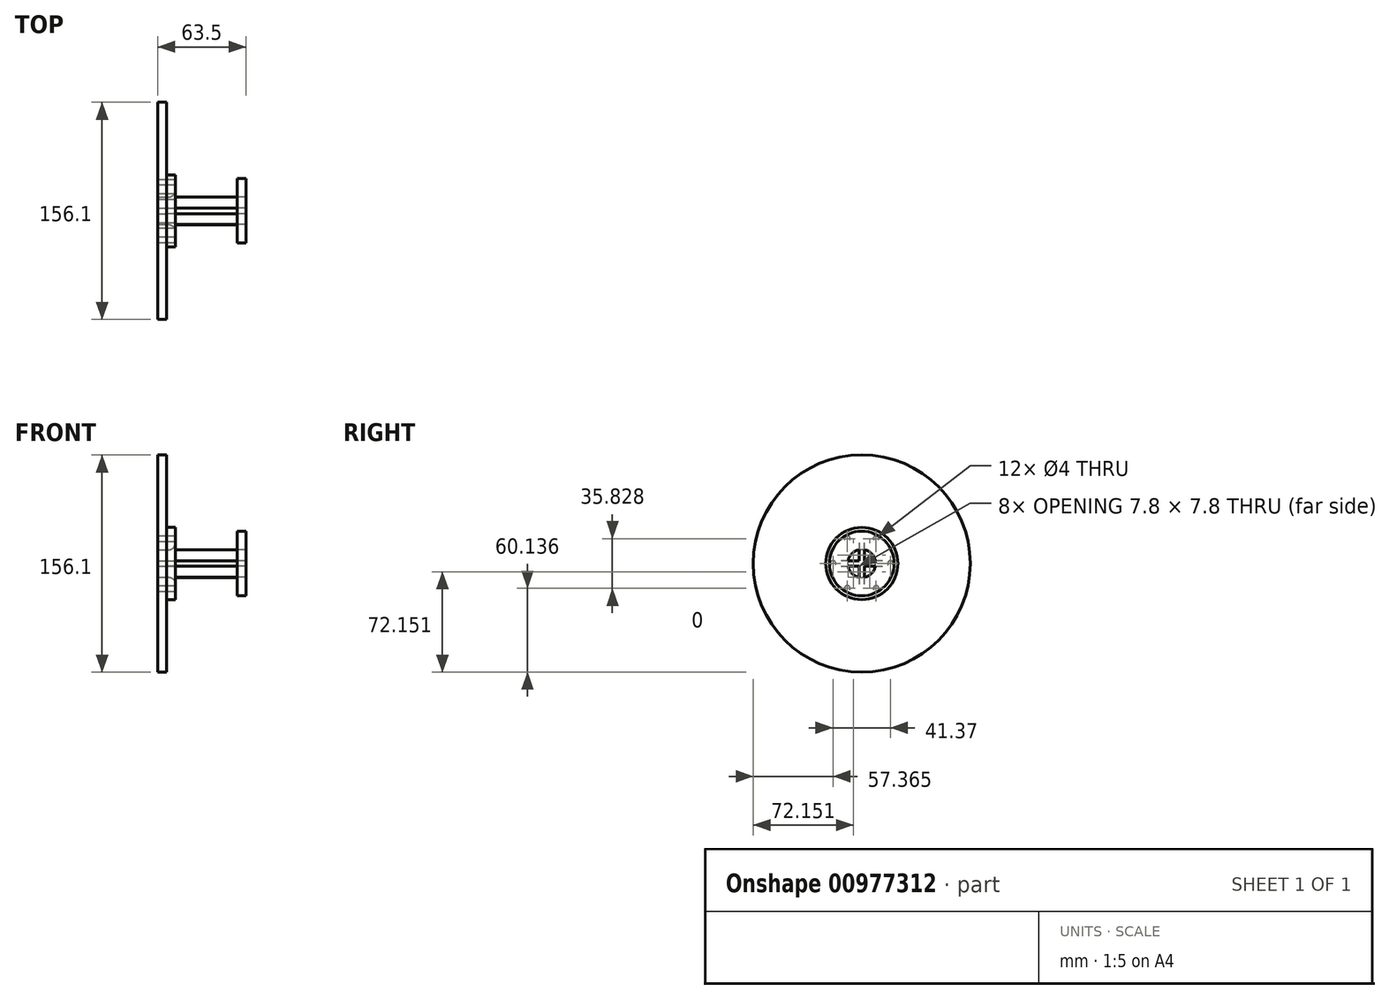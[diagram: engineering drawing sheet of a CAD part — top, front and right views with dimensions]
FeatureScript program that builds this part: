
annotation { "Feature Type Name" : "Feature", "Feature Type Description" : "" }
export const myFeature = defineFeature(function(context is Context, id is Id, definition is map)
    precondition{}
    {
        {
            var Q0;
            Q0=qCreatedBy(makeId("Right.planeOp"),FACE);
            var sketch = newSketch(context, id + "F0", { "sketchPlane" : qUnion([Q0])});
            skCircle(sketch, "E0", {"center": v(0, 0) * mm, "radius": 10 * mm});
            skLineSegment(sketch, "E1.bottom", {"start": v(2, 12.5) * mm, "end": v(-2, 12.5) * mm});
            skLineSegment(sketch, "E1.top", {"start": v(2, -12.5) * mm, "end": v(-2, -12.5) * mm});
            skLineSegment(sketch, "E1.left", {"start": v(2, 12.5) * mm, "end": v(2, -12.5) * mm});
            skLineSegment(sketch, "E1.right", {"start": v(-2, 12.5) * mm, "end": v(-2, -12.5) * mm});
            skLineSegment(sketch, "E2.bottom", {"start": v(12.5, 2) * mm, "end": v(-12.5, 2) * mm});
            skLineSegment(sketch, "E2.top", {"start": v(12.5, -2) * mm, "end": v(-12.5, -2) * mm});
            skLineSegment(sketch, "E2.left", {"start": v(12.5, 2) * mm, "end": v(12.5, -2) * mm});
            skLineSegment(sketch, "E2.right", {"start": v(-12.5, 2) * mm, "end": v(-12.5, -2) * mm});
            skLineSegment(sketch, "E3.bottom", {"start": v(2, 8) * mm, "end": v(-2, 8) * mm});
            skLineSegment(sketch, "E3.top", {"start": v(2, -8) * mm, "end": v(-2, -8) * mm});
            skLineSegment(sketch, "E4", {"start": v(-8, 2) * mm, "end": v(-8, -2) * mm});
            skLineSegment(sketch, "E5", {"start": v(8, 2) * mm, "end": v(8, -2) * mm});
            skCircle(sketch, "E6", {"center": v(0, 0) * mm, "radius": 25.94 * mm});
            skPoint(sketch, "E7", {"position": v(32.91, 0) * mm});
            skPoint(sketch, "E8", {"position": v(20.69, 0) * mm});
            skCircle(sketch, "E9.cCircle", {"center": v(0, 0) * mm, "radius": 20.69 * mm, "construction": true});
            skLineSegment(sketch, "E9.0", {"start": v(20.69, 0) * mm, "end": v(10.34, -17.91) * mm});
            skLineSegment(sketch, "E9.1", {"start": v(10.34, -17.91) * mm, "end": v(-10.34, -17.91) * mm});
            skLineSegment(sketch, "E9.2", {"start": v(-10.34, -17.91) * mm, "end": v(-20.69, 0) * mm});
            skLineSegment(sketch, "E9.3", {"start": v(-20.69, 0) * mm, "end": v(-10.34, 17.91) * mm});
            skLineSegment(sketch, "E9.4", {"start": v(-10.34, 17.91) * mm, "end": v(10.34, 17.91) * mm});
            skLineSegment(sketch, "E9.5", {"start": v(10.34, 17.91) * mm, "end": v(20.69, 0) * mm});
            skSolve(sketch);
        }
        {
            var Q0;
            {var subQ2=sQuery(id+"F0.wireOp",EDGE,"E0");var subQ4=sQuery(id+"F0.wireOp",EDGE,"E1.left");var subQ6=makeQuery(id+"F0.imprint","INTERSECT",VERTEX,{"disambiguationData":[OD(1.0)],"derivedFrom":[subQ2,subQ4]});Q0=makeQuery(id+"F0.imprint","IMPRINT",FACE,{"disambiguationData":[TD([[makeQuery(id+"F0.imprint","IMPRINT",EDGE,{"disambiguationData":[TD([[subQ6,-1.0]])],"derivedFrom":subQ2}),1.0]])]});}
            var Q1;
            {var subQ0=sQuery(id+"F0.wireOp",EDGE,"E2.top");var subQ5=sQuery(id+"F0.wireOp",EDGE,"E0");var subQ7=makeQuery(id+"F0.imprint","INTERSECT",VERTEX,{"disambiguationData":[OD(0.0)],"derivedFrom":[subQ5,subQ0]});Q1=makeQuery(id+"F0.imprint","IMPRINT",FACE,{"disambiguationData":[TD([[makeQuery(id+"F0.imprint","IMPRINT",EDGE,{"disambiguationData":[TD([[subQ7,-1.0]])],"derivedFrom":subQ5}),1.0]])]});}
            var Q2;
            {var subQ0=sQuery(id+"F0.wireOp",EDGE,"E1.right");var subQ5=sQuery(id+"F0.wireOp",EDGE,"E0");var subQ6=makeQuery(id+"F0.imprint","INTERSECT",VERTEX,{"disambiguationData":[OD(0.0)],"derivedFrom":[subQ5,subQ0]});Q2=makeQuery(id+"F0.imprint","IMPRINT",FACE,{"disambiguationData":[TD([[makeQuery(id+"F0.imprint","IMPRINT",EDGE,{"disambiguationData":[TD([[subQ6,-1.0]])],"derivedFrom":subQ5}),1.0]])]});}
            var Q3;
            {var subQ0=sQuery(id+"F0.wireOp",EDGE,"E1.left");var subQ4=sQuery(id+"F0.wireOp",EDGE,"E0");var subQ5=makeQuery(id+"F0.imprint","INTERSECT",VERTEX,{"disambiguationData":[OD(0.0)],"derivedFrom":[subQ4,subQ0]});Q3=makeQuery(id+"F0.imprint","IMPRINT",FACE,{"disambiguationData":[TD([[makeQuery(id+"F0.imprint","IMPRINT",EDGE,{"disambiguationData":[TD([[subQ5,1.0]])],"derivedFrom":subQ4}),1.0]])]});}
            var Q4;
            {var subQ5=sQuery(id+"F0.wireOp",EDGE,"E5");Q4=makeQuery(id+"F0.imprint","IMPRINT",FACE,{"disambiguationData":[TD([[makeQuery(id+"F0.imprint","IMPRINT",EDGE,{"derivedFrom":subQ5}),-1.0]])]});}
            var Q5;
            {var subQ0=sQuery(id+"F0.wireOp",EDGE,"E2.bottom");var subQ1=sQuery(id+"F0.wireOp",EDGE,"E1.left");var subQ2=makeQuery(id+"F0.imprint","INTERSECT",VERTEX,{"derivedFrom":[subQ1,subQ0]});Q5=makeQuery(id+"F0.imprint","IMPRINT",FACE,{"disambiguationData":[TD([[makeQuery(id+"F0.imprint","IMPRINT",EDGE,{"disambiguationData":[TD([[subQ2,-1.0]])],"derivedFrom":subQ1}),-1.0]])]});}
            var Q6;
            {var subQ0=sQuery(id+"F0.wireOp",EDGE,"E3.bottom");Q6=makeQuery(id+"F0.imprint","IMPRINT",FACE,{"disambiguationData":[TD([[makeQuery(id+"F0.imprint","IMPRINT",EDGE,{"derivedFrom":subQ0}),1.0]])]});}
            var Q7;
            {var subQ5=sQuery(id+"F0.wireOp",EDGE,"E4");Q7=makeQuery(id+"F0.imprint","IMPRINT",FACE,{"disambiguationData":[TD([[makeQuery(id+"F0.imprint","IMPRINT",EDGE,{"derivedFrom":subQ5}),1.0]])]});}
            var Q8;
            {var subQ0=sQuery(id+"F0.wireOp",EDGE,"E3.top");Q8=makeQuery(id+"F0.imprint","IMPRINT",FACE,{"disambiguationData":[TD([[makeQuery(id+"F0.imprint","IMPRINT",EDGE,{"derivedFrom":subQ0}),-1.0]])]});}
            var Q9;
            {var subQ5=sQuery(id+"F0.wireOp",EDGE,"E4");Q9=makeQuery(id+"F0.imprint","IMPRINT",FACE,{"disambiguationData":[TD([[makeQuery(id+"F0.imprint","IMPRINT",EDGE,{"derivedFrom":subQ5}),-1.0]])]});}
            var Q10;
            {var subQ5=sQuery(id+"F0.wireOp",EDGE,"E3.top");Q10=makeQuery(id+"F0.imprint","IMPRINT",FACE,{"disambiguationData":[TD([[makeQuery(id+"F0.imprint","IMPRINT",EDGE,{"derivedFrom":subQ5}),1.0]])]});}
            var Q11;
            {var subQ5=sQuery(id+"F0.wireOp",EDGE,"E5");Q11=makeQuery(id+"F0.imprint","IMPRINT",FACE,{"disambiguationData":[TD([[makeQuery(id+"F0.imprint","IMPRINT",EDGE,{"derivedFrom":subQ5}),1.0]])]});}
            var Q12;
            {var subQ5=sQuery(id+"F0.wireOp",EDGE,"E3.bottom");Q12=makeQuery(id+"F0.imprint","IMPRINT",FACE,{"disambiguationData":[TD([[makeQuery(id+"F0.imprint","IMPRINT",EDGE,{"derivedFrom":subQ5}),-1.0]])]});}
            extrude(context, id + "F1", {"entities" : qUnion([Q0, Q1, Q2, Q3, Q4, Q5, Q6, Q7, Q8, Q9, Q10, Q11, Q12]), "depth" : 50.8 * mm, "offsetDistance" : 25.4 * mm});
        }
        {
            var Q0;
            {var subQ10=sQuery(id+"F0.wireOp",EDGE,"E1.bottom");Q0=makeQuery(id+"F0.imprint","IMPRINT",FACE,{"disambiguationData":[TD([[makeQuery(id+"F0.imprint","IMPRINT",EDGE,{"derivedFrom":subQ10}),-1.0]])]});}
            var Q1;
            Q1=makeQuery(id+"F0.imprint","IMPRINT",FACE,{"disambiguationData":[TD([[makeQuery(id+"F0.imprint","IMPRINT",EDGE,{"derivedFrom":sQuery(id+"F0.wireOp",EDGE,"E6")}),1.0]])]});
            var Q2;
            {var subQ5=sQuery(id+"F0.wireOp",EDGE,"E1.bottom");Q2=makeQuery(id+"F0.imprint","IMPRINT",FACE,{"disambiguationData":[TD([[makeQuery(id+"F0.imprint","IMPRINT",EDGE,{"derivedFrom":subQ5}),1.0]])]});}
            var Q3;
            {var subQ5=sQuery(id+"F0.wireOp",EDGE,"E2.left");Q3=makeQuery(id+"F0.imprint","IMPRINT",FACE,{"disambiguationData":[TD([[makeQuery(id+"F0.imprint","IMPRINT",EDGE,{"derivedFrom":subQ5}),-1.0]])]});}
            var Q4;
            {var subQ5=sQuery(id+"F0.wireOp",EDGE,"E2.right");Q4=makeQuery(id+"F0.imprint","IMPRINT",FACE,{"disambiguationData":[TD([[makeQuery(id+"F0.imprint","IMPRINT",EDGE,{"derivedFrom":subQ5}),1.0]])]});}
            var Q5;
            {var subQ5=sQuery(id+"F0.wireOp",EDGE,"E1.top");Q5=makeQuery(id+"F0.imprint","IMPRINT",FACE,{"disambiguationData":[TD([[makeQuery(id+"F0.imprint","IMPRINT",EDGE,{"derivedFrom":subQ5}),-1.0]])]});}
            extrude(context, id + "F2", {"entities" : qUnion([Q0, Q1, Q2, Q3, Q4, Q5]), "operationType" : NewBodyOperationType.ADD, "depth" : 6.35 * mm, "offsetDistance" : 25.4 * mm});
        }
        {
            var Q0;
            {var subQ0=sQuery(id+"F0.wireOp",EDGE,"E0");Q0=makeQuery(id+"F2.boolean.opBoolean","MERGE",FACE,{"derivedFrom":[makeQuery(id+"F1.opExtrude","CAP_FACE",FACE,{"disambiguationData":[OSD([subQ0])],"isStart":true}),makeQuery(id+"F2.opExtrude","CAP_FACE",FACE,{"disambiguationData":[OSD([subQ0,sQuery(id+"F0.wireOp",EDGE,"E6")])],"isStart":true})]});}
            var sketch = newSketch(context, id + "F3", { "sketchPlane" : qUnion([Q0])});
            skCircle(sketch, "E10", {"center": v(0, 0) * mm, "radius": 78.05 * mm});
            skSolve(sketch);
        }
        {
            var Q0;
            Q0=makeQuery(id+"F3.imprint","IMPRINT",FACE,{"disambiguationData":[TD([[makeQuery(id+"F3.imprint","IMPRINT",EDGE,{"derivedFrom":sQuery(id+"F3.wireOp",EDGE,"E10")}),1.0]])]});
            var Q1;
            Q1=makeQuery(id+"F3.imprint","IMPRINT",FACE,{"disambiguationData":[TD([[makeQuery(id+"F3.imprint","IMPRINT",EDGE,{"derivedFrom":makeQuery(id+"F2.opExtrude","CAP_EDGE",EDGE,{"disambiguationData":[OSD([sQuery(id+"F0.wireOp",EDGE,"E6")])],"isStart":true})}),-1.0]])]});
            extrude(context, id + "F4", {"entities" : qUnion([Q0, Q1]), "depth" : 6.35 * mm, "offsetDistance" : 25.4 * mm});
        }
        {
            var Q0;
            Q0=makeQuery(id+"F1.opExtrude","CAP_FACE",FACE,{"disambiguationData":[OSD([sQuery(id+"F0.wireOp",EDGE,"E0")])],"isStart":false});
            var sketch = newSketch(context, id + "F5", { "sketchPlane" : qUnion([Q0])});
            skCircle(sketch, "E11", {"center": v(0, 0) * mm, "radius": 10 * mm});
            skLineSegment(sketch, "E12.bottom", {"start": v(2, 12.5) * mm, "end": v(-2, 12.5) * mm});
            skLineSegment(sketch, "E12.top", {"start": v(2, -12.5) * mm, "end": v(-2, -12.5) * mm});
            skLineSegment(sketch, "E12.left", {"start": v(2, 12.5) * mm, "end": v(2, -12.5) * mm});
            skLineSegment(sketch, "E12.right", {"start": v(-2, 12.5) * mm, "end": v(-2, -12.5) * mm});
            skLineSegment(sketch, "E13.bottom", {"start": v(12.5, 2) * mm, "end": v(-12.5, 2) * mm});
            skLineSegment(sketch, "E13.top", {"start": v(12.5, -2) * mm, "end": v(-12.5, -2) * mm});
            skLineSegment(sketch, "E13.left", {"start": v(12.5, 2) * mm, "end": v(12.5, -2) * mm});
            skLineSegment(sketch, "E13.right", {"start": v(-12.5, 2) * mm, "end": v(-12.5, -2) * mm});
            skLineSegment(sketch, "E14.bottom", {"start": v(2, 8) * mm, "end": v(-2, 8) * mm});
            skLineSegment(sketch, "E14.top", {"start": v(2, -8) * mm, "end": v(-2, -8) * mm});
            skLineSegment(sketch, "E15", {"start": v(-8, 2) * mm, "end": v(-8, -2) * mm});
            skLineSegment(sketch, "E16", {"start": v(8, 2) * mm, "end": v(8, -2) * mm});
            skCircle(sketch, "E17", {"center": v(0, 0) * mm, "radius": 23.23 * mm});
            skPoint(sketch, "E18", {"position": v(31.41, -0.52) * mm});
            skPoint(sketch, "E19", {"position": v(20.69, 0) * mm});
            skCircle(sketch, "E20.cCircle", {"center": v(0, 0) * mm, "radius": 20.69 * mm, "construction": true});
            skLineSegment(sketch, "E20.0", {"start": v(20.69, 0) * mm, "end": v(10.34, -17.91) * mm});
            skLineSegment(sketch, "E20.1", {"start": v(10.34, -17.91) * mm, "end": v(-10.34, -17.91) * mm});
            skLineSegment(sketch, "E20.2", {"start": v(-10.34, -17.91) * mm, "end": v(-20.69, 0) * mm});
            skLineSegment(sketch, "E20.3", {"start": v(-20.69, 0) * mm, "end": v(-10.34, 17.91) * mm});
            skLineSegment(sketch, "E20.4", {"start": v(-10.34, 17.91) * mm, "end": v(10.34, 17.91) * mm});
            skLineSegment(sketch, "E20.5", {"start": v(10.34, 17.91) * mm, "end": v(20.69, 0) * mm});
            skSolve(sketch);
        }
        {
            var Q0;
            {var subQ10=sQuery(id+"F5.wireOp",EDGE,"E12.bottom");Q0=makeQuery(id+"F5.imprint","IMPRINT",FACE,{"disambiguationData":[TD([[makeQuery(id+"F5.imprint","IMPRINT",EDGE,{"derivedFrom":subQ10}),-1.0]])]});}
            var Q1;
            {var subQ5=sQuery(id+"F5.wireOp",EDGE,"E12.bottom");Q1=makeQuery(id+"F5.imprint","IMPRINT",FACE,{"disambiguationData":[TD([[makeQuery(id+"F5.imprint","IMPRINT",EDGE,{"derivedFrom":subQ5}),1.0]])]});}
            var Q2;
            {var subQ5=sQuery(id+"F5.wireOp",EDGE,"E14.bottom");Q2=makeQuery(id+"F5.imprint","IMPRINT",FACE,{"disambiguationData":[TD([[makeQuery(id+"F5.imprint","IMPRINT",EDGE,{"derivedFrom":subQ5}),-1.0]])]});}
            var Q3;
            {var subQ0=sQuery(id+"F5.wireOp",EDGE,"E14.bottom");Q3=makeQuery(id+"F5.imprint","IMPRINT",FACE,{"disambiguationData":[TD([[makeQuery(id+"F5.imprint","IMPRINT",EDGE,{"derivedFrom":subQ0}),1.0]])]});}
            var Q4;
            {var subQ0=sQuery(id+"F5.wireOp",EDGE,"E12.left");var subQ4=sQuery(id+"F5.wireOp",EDGE,"E11");var subQ5=makeQuery(id+"F5.imprint","INTERSECT",VERTEX,{"disambiguationData":[OD(0.0)],"derivedFrom":[subQ4,subQ0]});Q4=makeQuery(id+"F5.imprint","IMPRINT",FACE,{"disambiguationData":[TD([[makeQuery(id+"F5.imprint","IMPRINT",EDGE,{"disambiguationData":[TD([[subQ5,1.0]])],"derivedFrom":subQ4}),1.0]])]});}
            var Q5;
            {var subQ5=sQuery(id+"F5.wireOp",EDGE,"E16");Q5=makeQuery(id+"F5.imprint","IMPRINT",FACE,{"disambiguationData":[TD([[makeQuery(id+"F5.imprint","IMPRINT",EDGE,{"derivedFrom":subQ5}),-1.0]])]});}
            var Q6;
            {var subQ5=sQuery(id+"F5.wireOp",EDGE,"E16");Q6=makeQuery(id+"F5.imprint","IMPRINT",FACE,{"disambiguationData":[TD([[makeQuery(id+"F5.imprint","IMPRINT",EDGE,{"derivedFrom":subQ5}),1.0]])]});}
            var Q7;
            {var subQ5=sQuery(id+"F5.wireOp",EDGE,"E13.left");Q7=makeQuery(id+"F5.imprint","IMPRINT",FACE,{"disambiguationData":[TD([[makeQuery(id+"F5.imprint","IMPRINT",EDGE,{"derivedFrom":subQ5}),-1.0]])]});}
            var Q8;
            {var subQ2=sQuery(id+"F5.wireOp",EDGE,"E11");var subQ4=sQuery(id+"F5.wireOp",EDGE,"E12.left");var subQ6=makeQuery(id+"F5.imprint","INTERSECT",VERTEX,{"disambiguationData":[OD(1.0)],"derivedFrom":[subQ2,subQ4]});Q8=makeQuery(id+"F5.imprint","IMPRINT",FACE,{"disambiguationData":[TD([[makeQuery(id+"F5.imprint","IMPRINT",EDGE,{"disambiguationData":[TD([[subQ6,-1.0]])],"derivedFrom":subQ2}),1.0]])]});}
            var Q9;
            {var subQ0=sQuery(id+"F5.wireOp",EDGE,"E14.top");Q9=makeQuery(id+"F5.imprint","IMPRINT",FACE,{"disambiguationData":[TD([[makeQuery(id+"F5.imprint","IMPRINT",EDGE,{"derivedFrom":subQ0}),-1.0]])]});}
            var Q10;
            {var subQ0=sQuery(id+"F5.wireOp",EDGE,"E13.bottom");var subQ1=sQuery(id+"F5.wireOp",EDGE,"E12.left");var subQ2=makeQuery(id+"F5.imprint","INTERSECT",VERTEX,{"derivedFrom":[subQ1,subQ0]});Q10=makeQuery(id+"F5.imprint","IMPRINT",FACE,{"disambiguationData":[TD([[makeQuery(id+"F5.imprint","IMPRINT",EDGE,{"disambiguationData":[TD([[subQ2,-1.0]])],"derivedFrom":subQ1}),-1.0]])]});}
            var Q11;
            {var subQ5=sQuery(id+"F5.wireOp",EDGE,"E12.top");Q11=makeQuery(id+"F5.imprint","IMPRINT",FACE,{"disambiguationData":[TD([[makeQuery(id+"F5.imprint","IMPRINT",EDGE,{"derivedFrom":subQ5}),-1.0]])]});}
            var Q12;
            {var subQ5=sQuery(id+"F5.wireOp",EDGE,"E14.top");Q12=makeQuery(id+"F5.imprint","IMPRINT",FACE,{"disambiguationData":[TD([[makeQuery(id+"F5.imprint","IMPRINT",EDGE,{"derivedFrom":subQ5}),1.0]])]});}
            var Q13;
            {var subQ0=sQuery(id+"F5.wireOp",EDGE,"E13.top");var subQ5=sQuery(id+"F5.wireOp",EDGE,"E11");var subQ7=makeQuery(id+"F5.imprint","INTERSECT",VERTEX,{"disambiguationData":[OD(0.0)],"derivedFrom":[subQ5,subQ0]});Q13=makeQuery(id+"F5.imprint","IMPRINT",FACE,{"disambiguationData":[TD([[makeQuery(id+"F5.imprint","IMPRINT",EDGE,{"disambiguationData":[TD([[subQ7,-1.0]])],"derivedFrom":subQ5}),1.0]])]});}
            var Q14;
            {var subQ5=sQuery(id+"F5.wireOp",EDGE,"E15");Q14=makeQuery(id+"F5.imprint","IMPRINT",FACE,{"disambiguationData":[TD([[makeQuery(id+"F5.imprint","IMPRINT",EDGE,{"derivedFrom":subQ5}),1.0]])]});}
            var Q15;
            {var subQ0=sQuery(id+"F5.wireOp",EDGE,"E12.right");var subQ5=sQuery(id+"F5.wireOp",EDGE,"E11");var subQ6=makeQuery(id+"F5.imprint","INTERSECT",VERTEX,{"disambiguationData":[OD(0.0)],"derivedFrom":[subQ5,subQ0]});Q15=makeQuery(id+"F5.imprint","IMPRINT",FACE,{"disambiguationData":[TD([[makeQuery(id+"F5.imprint","IMPRINT",EDGE,{"disambiguationData":[TD([[subQ6,-1.0]])],"derivedFrom":subQ5}),1.0]])]});}
            var Q16;
            {var subQ5=sQuery(id+"F5.wireOp",EDGE,"E15");Q16=makeQuery(id+"F5.imprint","IMPRINT",FACE,{"disambiguationData":[TD([[makeQuery(id+"F5.imprint","IMPRINT",EDGE,{"derivedFrom":subQ5}),-1.0]])]});}
            var Q17;
            {var subQ5=sQuery(id+"F5.wireOp",EDGE,"E13.right");Q17=makeQuery(id+"F5.imprint","IMPRINT",FACE,{"disambiguationData":[TD([[makeQuery(id+"F5.imprint","IMPRINT",EDGE,{"derivedFrom":subQ5}),1.0]])]});}
            var Q18;
            Q18=makeQuery(id+"F5.imprint","IMPRINT",FACE,{"disambiguationData":[TD([[makeQuery(id+"F5.imprint","IMPRINT",EDGE,{"derivedFrom":sQuery(id+"F5.wireOp",EDGE,"E17")}),1.0]])]});
            extrude(context, id + "F6", {"entities" : qUnion([Q0, Q1, Q2, Q3, Q4, Q5, Q6, Q7, Q8, Q9, Q10, Q11, Q12, Q13, Q14, Q15, Q16, Q17, Q18]), "operationType" : NewBodyOperationType.ADD, "depth" : 6.35 * mm, "offsetDistance" : 25.4 * mm});
        }
        {
            var Q0;
            Q0=makeQuery(id+"F2.opExtrude","CAP_EDGE",EDGE,{"disambiguationData":[OSD([sQuery(id+"F0.wireOp",EDGE,"E0")])],"isStart":false});
            fillet(context, id + "F7", {"entities" : qUnion([Q0]), "radius" : 5.08 * mm, "tangentPropagation" : true, "allowEdgeOverflow" : false});
        }
        {
            var Q0;
            Q0=sQuery(id+"F5.wireOp",VERTEX,"E20.4.end");
            var Q1;
            Q1=sQuery(id+"F5.wireOp",VERTEX,"E19");
            var Q2;
            Q2=sQuery(id+"F5.wireOp",VERTEX,"E20.3.end");
            var Q3;
            Q3=sQuery(id+"F5.wireOp",VERTEX,"E20.0.end");
            var Q4;
            Q4=sQuery(id+"F5.wireOp",VERTEX,"E20.1.end");
            var Q5;
            Q5=sQuery(id+"F5.wireOp",VERTEX,"E20.2.end");
            var Q6;
            Q6=makeQuery(id+"F1.opExtrude","SWEPT_BODY",BODY,{"disambiguationData":[OSD([sQuery(id+"F0.wireOp",EDGE,"E0")])]});
            var Q7;
            Q7=makeQuery(id+"F4.opExtrude","SWEPT_BODY",BODY,{"disambiguationData":[OSD([sQuery(id+"F3.wireOp",EDGE,"E10")])]});
            hole(context, id + "F8", {"style" : HoleStyle.SIMPLE, "endStyle" : HoleEndStyle.THROUGH, "holeDiameter" : 4 * mm, "majorDiameter" : 6.35 * mm, "isTappedThrough" : true, "tappedDepth" : 12.7 * mm, "tapClearance" : 3, "startFromSketch" : true, "locations" : qUnion([Q0, Q1, Q2, Q3, Q4, Q5]), "scope" : qUnion([Q6, Q7])});
        }
    });
